# Revit family: 979110001_Llave Jardin Palanca
name_source: partatom
category: Plumbing Fixtures
units: mm (PartAtom-declared; Revit-internal decimal feet)

## family parameters
Always vertical = Yes
Cut with Voids When Loaded = No
Part Type = Normal
Room Calculation Point = No
Round Connector Dimension = Use Diameter
Shared = No
Work Plane-Based = No

## types (1)
- 979110001_Llave Jardin Palanca
    Ancho = 50 mm  [stored 0.164042 ft]
    Capacidad de flujo = 15 L/min a 20 PSI.
    Creado por = IDD
    Description = • Acabado satinado y Robusto.
• Ideal para trabajo pesado.
• Calidad GRIVAL, que nos permite ofrecer una garantía de 5 años.
• Accionamiento palanca.
• Incluye escudo.
    Fecha de creación = 12/08/2020
    Manufacturer = Corona
    Material = Corona_Laton
    Peso Bruto aprox = 270gr. / 0.5952 Lb.
    Peso neto = 265gr. / 0.5842 Lb.
    Presion maxima = 125 psi.
    Presion minima = 20 psi.
    Profundidad = 148 mm

note: [stored X ft] marks values corroborated as IEEE doubles in the binary element streams (Revit-internal decimal feet)

## geometry (parser evidence)
native form markers: Sweep x2
no freeform markers — native parametric forms only
